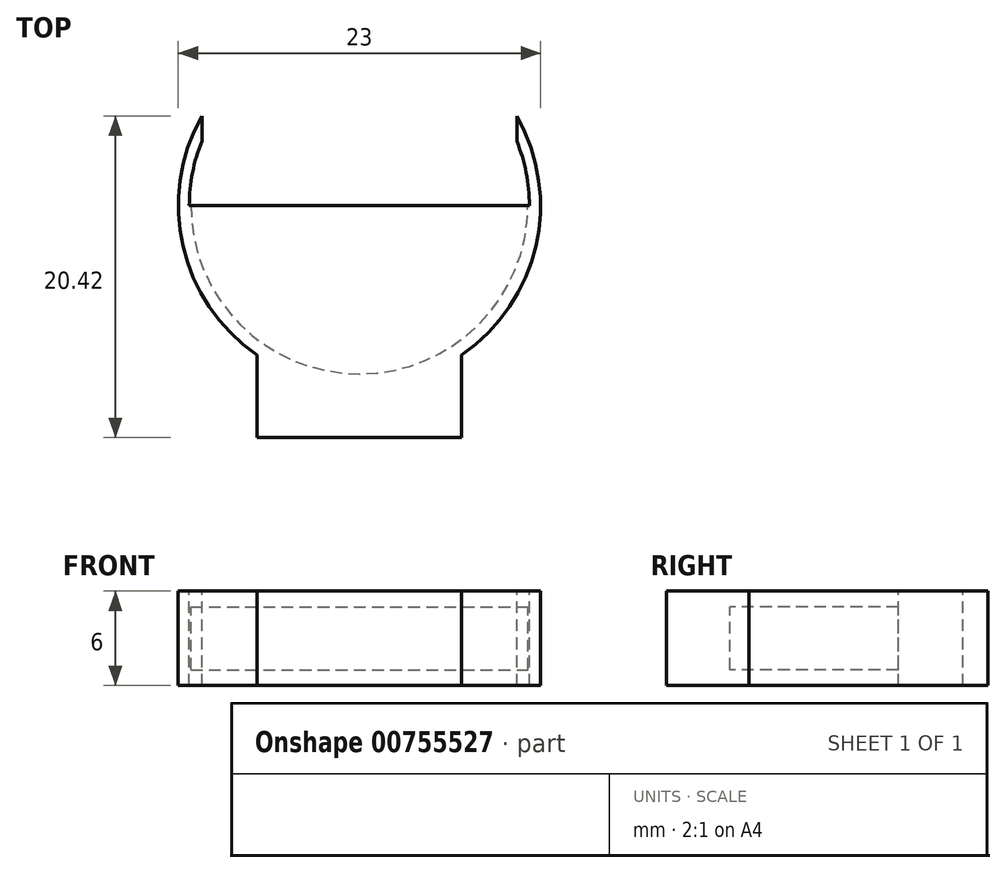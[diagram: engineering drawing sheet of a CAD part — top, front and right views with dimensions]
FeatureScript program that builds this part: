
annotation { "Feature Type Name" : "Feature", "Feature Type Description" : "" }
export const myFeature = defineFeature(function(context is Context, id is Id, definition is map)
    precondition{}
    {
        {
            var Q0;
            Q0=qCreatedBy(makeId("Top.planeOp"),FACE);
            var sketch = newSketch(context, id + "F0", { "sketchPlane" : qUnion([Q0])});
            skCircle(sketch, "E0", {"center": v(0, 0) * mm, "radius": 11.5 * mm});
            skLineSegment(sketch, "E1", {"start": v(-6.5, -9.49) * mm, "end": v(6.5, -9.49) * mm, "construction": true});
            skLineSegment(sketch, "E2", {"start": v(6.5, -9.49) * mm, "end": v(6.5, -14.74) * mm});
            skLineSegment(sketch, "E3", {"start": v(6.5, -14.74) * mm, "end": v(-6.5, -14.74) * mm});
            skLineSegment(sketch, "E4", {"start": v(-6.5, -14.74) * mm, "end": v(-6.5, -9.49) * mm});
            skArc(sketch, "E5", {"start": v(-4.5, -9.49) * mm, "mid": v(0, -10.5) * mm, "end": v(4.5, -9.49) * mm});
            skSolve(sketch);
        }
        {
            var Q0;
            Q0 = qSketchRegion(id + "F0", true);
            extrude(context, id + "F1", {"entities" : qUnion([Q0]), "endBound" : BoundingType.SYMMETRIC, "depth" : 6 * mm, "offsetDistance" : 25 * mm});
        }
        {
            var Q0;
            Q0=qCreatedBy(makeId("Top.planeOp"),FACE);
            var sketch = newSketch(context, id + "F2", { "sketchPlane" : qUnion([Q0])});
            skCircle(sketch, "E6", {"center": v(0, 0) * mm, "radius": 10.7 * mm});
            skSolve(sketch);
        }
        {
            var Q0;
            Q0 = qSketchRegion(id + "F2", true);
            extrude(context, id + "F3", {"entities" : qUnion([Q0]), "operationType" : NewBodyOperationType.REMOVE, "endBound" : BoundingType.SYMMETRIC, "oppositeDirection" : true, "depth" : 4 * mm, "offsetDistance" : 25 * mm});
        }
        {
            var Q0;
            Q0=makeQuery(id+"F1.opExtrude","CAP_FACE",FACE,{"disambiguationData":[OSD([sQuery(id+"F0.wireOp",EDGE,"E0"),sQuery(id+"F0.wireOp",EDGE,"E2"),sQuery(id+"F0.wireOp",EDGE,"E3"),sQuery(id+"F0.wireOp",EDGE,"E4")])],"isStart":false});
            var sketch = newSketch(context, id + "F4", { "sketchPlane" : qUnion([Q0])});
            skArc(sketch, "E7", {"start": v(10.8, 0) * mm, "mid": v(10.6, 2.08) * mm, "end": v(10, 4.08) * mm});
            skLineSegment(sketch, "E8", {"start": v(-10.8, 0) * mm, "end": v(10.8, 0) * mm, "construction": true});
            skLineSegment(sketch, "E9", {"start": v(0, 11.5) * mm, "end": v(0, -11.5) * mm, "construction": true});
            skPoint(sketch, "E9.endSnap0", {"position": v(0, 11.5) * mm});
            skLineSegment(sketch, "E10", {"start": v(-10.8, 0) * mm, "end": v(10.8, 0) * mm});
            skLineSegment(sketch, "E11", {"start": v(-10, 4.08) * mm, "end": v(-10, 14.08) * mm});
            skLineSegment(sketch, "E12", {"start": v(10, 4.08) * mm, "end": v(10, 14.08) * mm});
            skLineSegment(sketch, "E13", {"start": v(10, 14.08) * mm, "end": v(-10, 14.08) * mm});
            skLineSegment(sketch, "E14", {"start": v(-10, 4.08) * mm, "end": v(10, 4.08) * mm, "construction": true});
            skArc(sketch, "E15.trimOffspring", {"start": v(-10, 4.08) * mm, "mid": v(-10.6, 2.08) * mm, "end": v(-10.8, 0) * mm});
            skSolve(sketch);
        }
        {
            var Q0;
            Q0=makeQuery(id+"F4.imprint","IMPRINT",FACE,{"disambiguationData":[TD([[makeQuery(id+"F4.imprint","IMPRINT",EDGE,{"derivedFrom":sQuery(id+"F4.wireOp",EDGE,"E7")}),1.0]])]});
            extrude(context, id + "F5", {"entities" : qUnion([Q0]), "operationType" : NewBodyOperationType.REMOVE, "endBound" : BoundingType.THROUGH_ALL, "oppositeDirection" : true, "depth" : 25 * mm, "offsetDistance" : 25 * mm});
        }
    });
